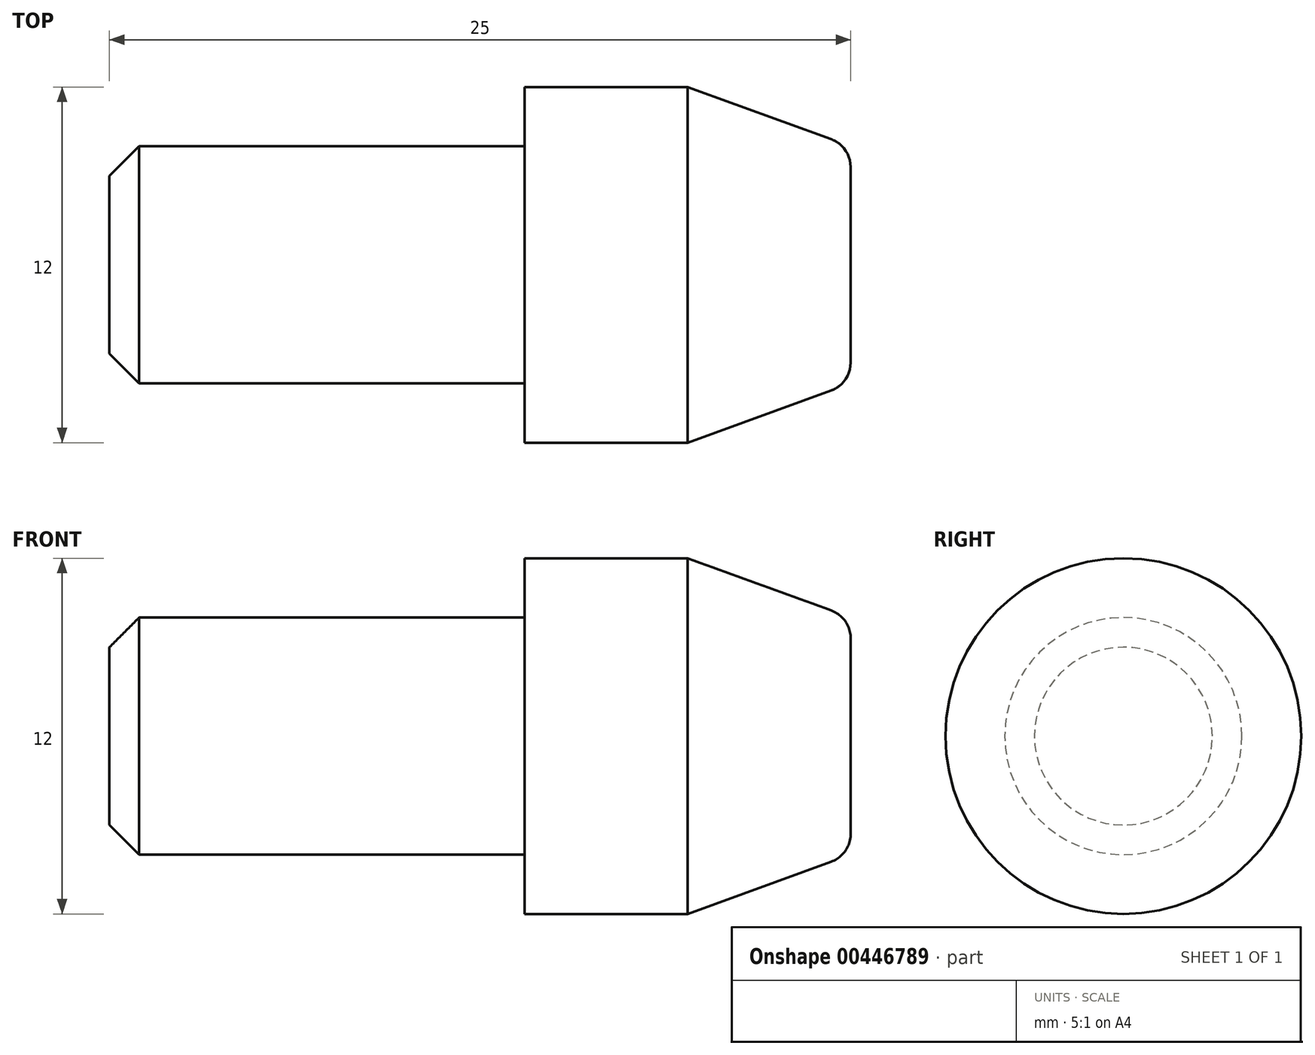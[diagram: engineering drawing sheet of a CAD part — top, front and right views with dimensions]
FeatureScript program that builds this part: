
annotation { "Feature Type Name" : "Feature", "Feature Type Description" : "" }
export const myFeature = defineFeature(function(context is Context, id is Id, definition is map)
    precondition{}
    {
        {
            var Q0;
            Q0=qCreatedBy(makeId("Front.planeOp"),FACE);
            var sketch = newSketch(context, id + "F0", { "sketchPlane" : qUnion([Q0])});
            skLineSegment(sketch, "E0", {"start": v(-10.96, 0) * mm, "end": v(31.6, 0) * mm, "construction": true});
            skLineSegment(sketch, "E1", {"start": v(0, 0) * mm, "end": v(0, 4) * mm});
            skLineSegment(sketch, "E2", {"start": v(0, 4) * mm, "end": v(14, 4) * mm});
            skLineSegment(sketch, "E3", {"start": v(14, 4) * mm, "end": v(14, 6) * mm});
            skLineSegment(sketch, "E4", {"start": v(14, 6) * mm, "end": v(19.5, 6) * mm});
            skLineSegment(sketch, "E5", {"start": v(19.5, 6) * mm, "end": v(25, 4) * mm});
            skLineSegment(sketch, "E6", {"start": v(25, 4) * mm, "end": v(25, 0) * mm});
            skLineSegment(sketch, "E7", {"start": v(25, 0) * mm, "end": v(0, 0) * mm});
            skSolve(sketch);
        }
        {
            var Q0;
            Q0 = qSketchRegion(id + "F0", true);
            var Q1;
            Q1=sQuery(id+"F0.wireOp",EDGE,"E0");
            revolve(context, id + "F1", {"entities" : qUnion([Q0]), "axis" : qUnion([Q1]), "revolveType" : RevolveType.FULL});
        }
        {
            var Q0;
            Q0=makeQuery(id+"F1.opRevolve","SWEPT_EDGE",EDGE,{"disambiguationData":[OSD([sQuery(id+"F0.wireOp",EDGE,"E1"),sQuery(id+"F0.wireOp",EDGE,"E2")])]});
            chamfer(context, id + "F2", {"entities" : qUnion([Q0]), "width" : 1 * mm, "tangentPropagation" : true});
        }
        {
            var Q0;
            Q0=makeQuery(id+"F1.opRevolve","SWEPT_EDGE",EDGE,{"disambiguationData":[OSD([sQuery(id+"F0.wireOp",EDGE,"E5"),sQuery(id+"F0.wireOp",EDGE,"E6")])]});
            fillet(context, id + "F3", {"entities" : qUnion([Q0]), "radius" : 1 * mm, "tangentPropagation" : true, "allowEdgeOverflow" : false});
        }
    });
